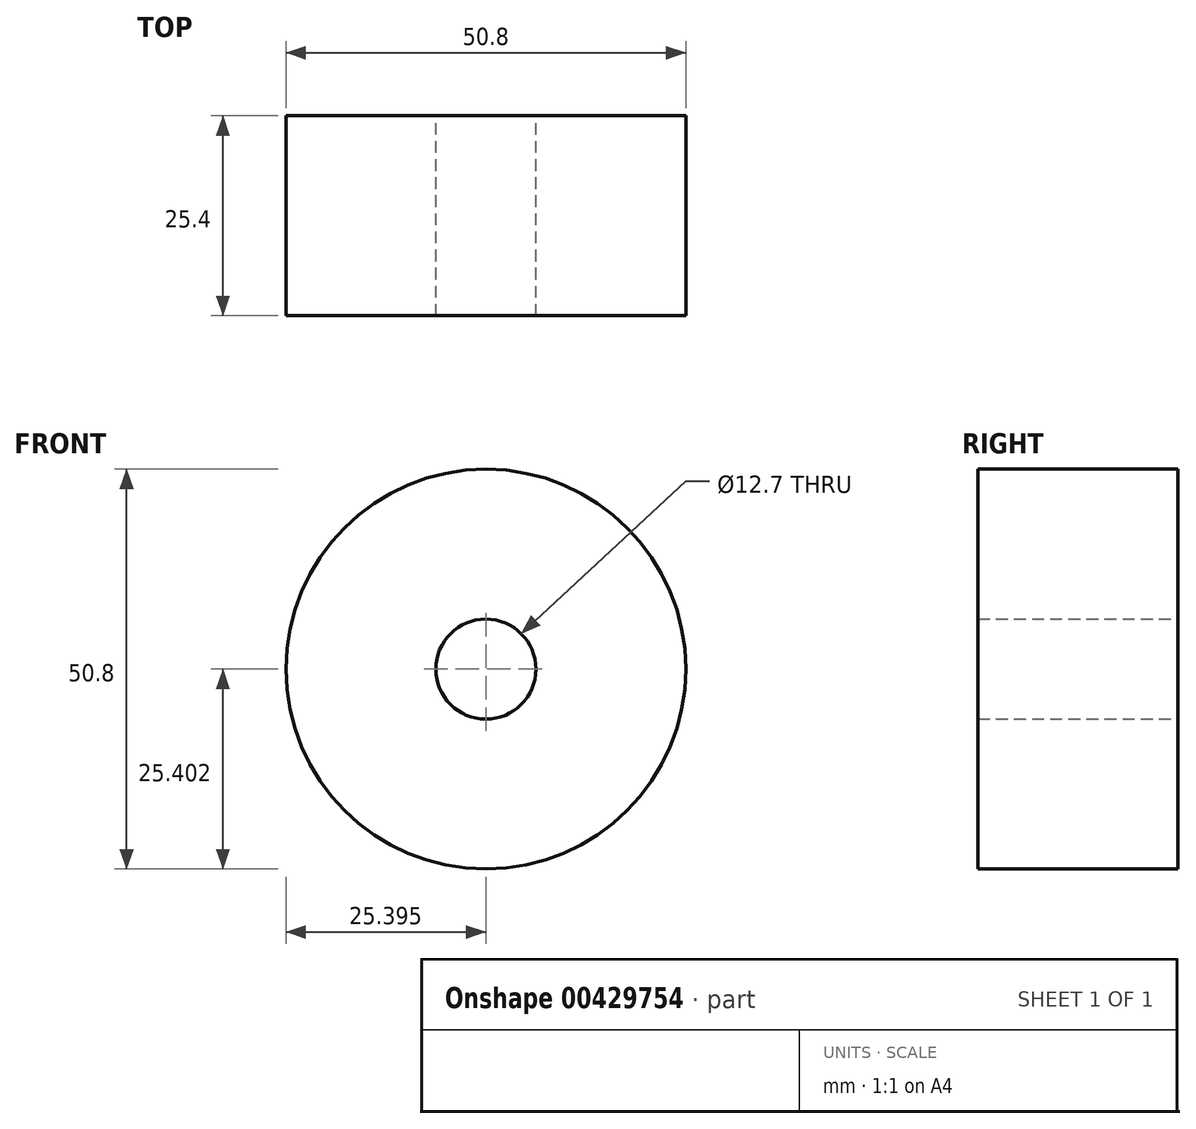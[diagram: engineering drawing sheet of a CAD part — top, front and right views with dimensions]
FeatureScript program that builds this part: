
annotation { "Feature Type Name" : "Feature", "Feature Type Description" : "" }
export const myFeature = defineFeature(function(context is Context, id is Id, definition is map)
    precondition{}
    {
        {
            var Q0;
            Q0=qCreatedBy(makeId("Front.planeOp"),FACE);
            var sketch = newSketch(context, id + "F0", { "sketchPlane" : qUnion([Q0])});
            skCircle(sketch, "E0", {"center": v(-55.93, 12.85) * mm, "radius": 25.4 * mm});
            skSolve(sketch);
        }
        {
            var Q0;
            Q0=makeQuery(id+"F0.imprint","IMPRINT",FACE,{"disambiguationData":[TD([[makeQuery(id+"F0.imprint","IMPRINT",EDGE,{"derivedFrom":sQuery(id+"F0.wireOp",EDGE,"E0")}),1.0]])]});
            extrude(context, id + "F1", {"entities" : qUnion([Q0]), "depth" : 25.4 * mm});
        }
        {
            var Q0;
            Q0=sQuery(id+"F0.wireOp",VERTEX,"E0.center");
            var Q1;
            Q1=makeQuery(id+"F1.opExtrude","SWEPT_BODY",BODY,{"disambiguationData":[OSD([sQuery(id+"F0.wireOp",EDGE,"E0")])]});
            hole(context, id + "F2", {"style" : HoleStyle.C_BORE, "endStyle" : HoleEndStyle.THROUGH, "oppositeDirection" : true, "holeDiameter" : 12.7 * mm, "cBoreDiameter" : 38.1 * mm, "cBoreDepth" : 0 * mm, "isTappedThrough" : true, "tappedDepth" : 12.7 * mm, "tapClearance" : 3, "startFromSketch" : true, "locations" : qUnion([Q0]), "scope" : qUnion([Q1])});
        }
    });
